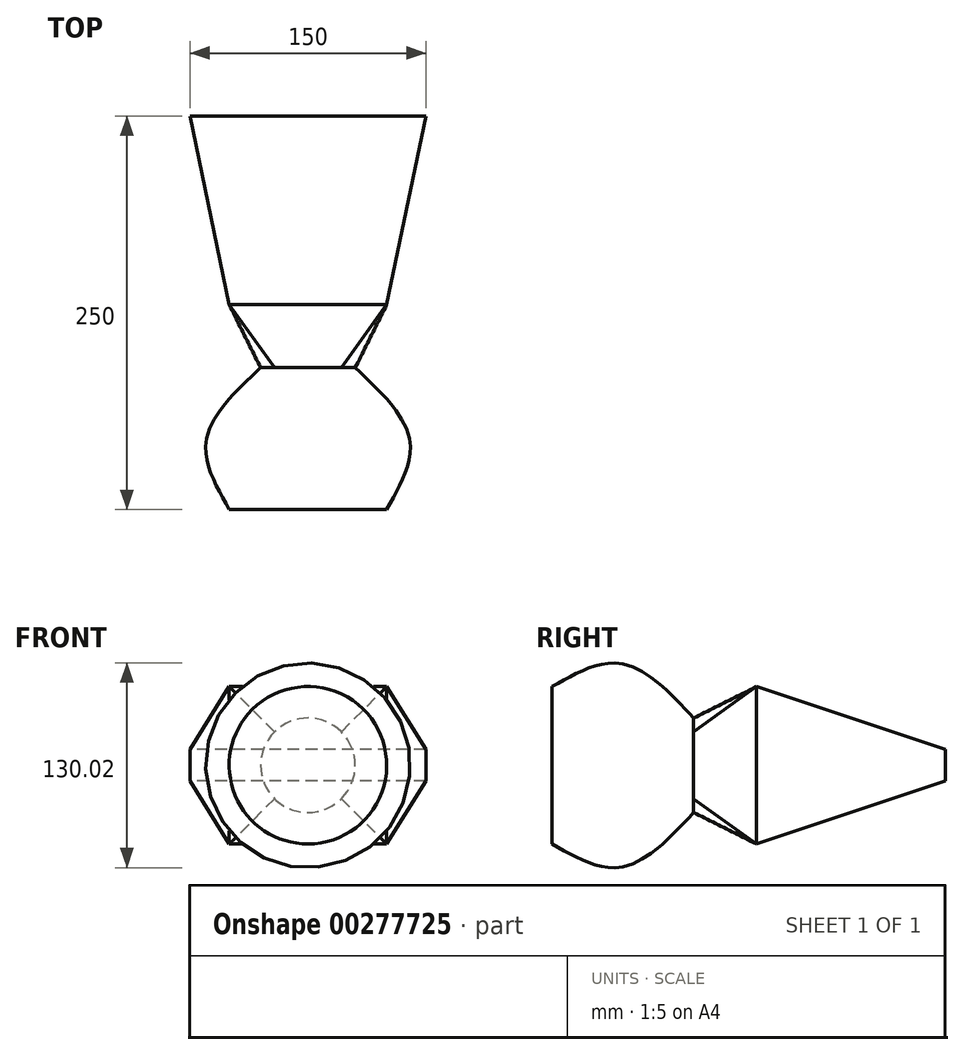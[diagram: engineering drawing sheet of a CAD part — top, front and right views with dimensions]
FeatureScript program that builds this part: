
annotation { "Feature Type Name" : "Feature", "Feature Type Description" : "" }
export const myFeature = defineFeature(function(context is Context, id is Id, definition is map)
    precondition{}
    {
        {
            var Q0;
            Q0=qCreatedBy(makeId("Front.planeOp"),FACE);
            var sketch = newSketch(context, id + "F0", { "sketchPlane" : qUnion([Q0])});
            skCircle(sketch, "E0", {"center": v(0, 0) * mm, "radius": 50 * mm});
            skSolve(sketch);
        }
        {
            var Q0;
            Q0=qCreatedBy(makeId("Front.planeOp"),FACE);
            cPlane(context, id + "F1", {"entities" : qUnion([Q0]), "cplaneType" : CPlaneType.OFFSET, "offset" : 40 * mm, "oppositeDirection" : true, "width" : 150 * mm, "height" : 150 * mm});
        }
        {
            var Q0;
            Q0=qCreatedBy(id+"F1.planeOp",FACE);
            var sketch = newSketch(context, id + "F2", { "sketchPlane" : qUnion([Q0])});
            skCircle(sketch, "E1", {"center": v(0, 0) * mm, "radius": 65 * mm});
            skSolve(sketch);
        }
        {
            var Q0;
            Q0=qCreatedBy(id+"F1.planeOp",FACE);
            cPlane(context, id + "F3", {"entities" : qUnion([Q0]), "cplaneType" : CPlaneType.OFFSET, "offset" : 50 * mm, "oppositeDirection" : true, "width" : 150 * mm, "height" : 150 * mm});
        }
        {
            var Q0;
            Q0=qCreatedBy(id+"F3.planeOp",FACE);
            var sketch = newSketch(context, id + "F4", { "sketchPlane" : qUnion([Q0])});
            skCircle(sketch, "E2", {"center": v(0, 0) * mm, "radius": 30 * mm});
            skSolve(sketch);
        }
        {
            var Q0;
            Q0=makeQuery(id+"F0.imprint","IMPRINT",FACE,{"disambiguationData":[TD([[makeQuery(id+"F0.imprint","IMPRINT",EDGE,{"derivedFrom":sQuery(id+"F0.wireOp",EDGE,"E0")}),1.0]])]});
            var Q1;
            Q1=makeQuery(id+"F2.imprint","IMPRINT",FACE,{"disambiguationData":[TD([[makeQuery(id+"F2.imprint","IMPRINT",EDGE,{"derivedFrom":sQuery(id+"F2.wireOp",EDGE,"E1")}),1.0]])]});
            var Q2;
            Q2=makeQuery(id+"F4.imprint","IMPRINT",FACE,{"disambiguationData":[TD([[makeQuery(id+"F4.imprint","IMPRINT",EDGE,{"derivedFrom":sQuery(id+"F4.wireOp",EDGE,"E2")}),1.0]])]});
            loft(context, id + "F5", {"sheetProfilesArray" : [{ "sheetProfileEntities" : qUnion([Q0]) }, { "sheetProfileEntities" : qUnion([Q1]) }, { "sheetProfileEntities" : qUnion([Q2]) }]});
        }
        {
            var Q0;
            Q0=qCreatedBy(id+"F3.planeOp",FACE);
            cPlane(context, id + "F6", {"entities" : qUnion([Q0]), "cplaneType" : CPlaneType.OFFSET, "offset" : 40 * mm, "oppositeDirection" : true, "width" : 150 * mm, "height" : 150 * mm});
        }
        {
            var Q0;
            Q0=qCreatedBy(id+"F6.planeOp",FACE);
            cPlane(context, id + "F7", {"entities" : qUnion([Q0]), "cplaneType" : CPlaneType.OFFSET, "offset" : 120 * mm, "oppositeDirection" : true, "width" : 150 * mm, "height" : 150 * mm});
        }
        {
            var Q0;
            Q0=qCreatedBy(id+"F6.planeOp",FACE);
            var sketch = newSketch(context, id + "F8", { "sketchPlane" : qUnion([Q0])});
            skLineSegment(sketch, "E3.bottom", {"start": v(50, -50) * mm, "end": v(-50, -50) * mm});
            skLineSegment(sketch, "E3.top", {"start": v(50, 50) * mm, "end": v(-50, 50) * mm});
            skLineSegment(sketch, "E3.left", {"start": v(50, -50) * mm, "end": v(50, 50) * mm});
            skLineSegment(sketch, "E3.right", {"start": v(-50, -50) * mm, "end": v(-50, 50) * mm});
            skPoint(sketch, "E3.middle", {"position": v(0, 0) * mm});
            skSolve(sketch);
        }
        {
            var Q0;
            Q0=qCreatedBy(id+"F7.planeOp",FACE);
            var sketch = newSketch(context, id + "F9", { "sketchPlane" : qUnion([Q0])});
            skLineSegment(sketch, "E4.bottom", {"start": v(75, 10) * mm, "end": v(-75, 10) * mm});
            skLineSegment(sketch, "E4.top", {"start": v(75, -10) * mm, "end": v(-75, -10) * mm});
            skLineSegment(sketch, "E4.left", {"start": v(75, 10) * mm, "end": v(75, -10) * mm});
            skLineSegment(sketch, "E4.right", {"start": v(-75, 10) * mm, "end": v(-75, -10) * mm});
            skPoint(sketch, "E4.middle", {"position": v(0, 0) * mm});
            skSolve(sketch);
        }
        {
            var Q1;
            Q1=makeQuery(id+"F5.opLoft","CAP_FACE",FACE,{"disambiguationData":[OSD([makeQuery(id+"F4.imprint","IMPRINT",FACE,{"disambiguationData":[TD([[makeQuery(id+"F4.imprint","IMPRINT",EDGE,{"derivedFrom":sQuery(id+"F4.wireOp",EDGE,"E2")}),1.0]])]})])],"isStart":true});
            var Q2;
            Q2=makeQuery(id+"F8.imprint","IMPRINT",FACE,{"disambiguationData":[TD([[makeQuery(id+"F8.imprint","IMPRINT",EDGE,{"derivedFrom":sQuery(id+"F8.wireOp",EDGE,"E3.bottom")}),-1.0]])]});
            loft(context, id + "F10", {"operationType" : NewBodyOperationType.ADD, "sheetProfilesArray" : [{ "sheetProfileEntities" : qUnion([Q1]) }, { "sheetProfileEntities" : qUnion([Q2]) }]});
        }
        {
            var Q1;
            Q1=makeQuery(id+"F10.opLoft","CAP_FACE",FACE,{"disambiguationData":[OSD([makeQuery(id+"F8.imprint","IMPRINT",FACE,{"disambiguationData":[TD([[makeQuery(id+"F8.imprint","IMPRINT",EDGE,{"derivedFrom":sQuery(id+"F8.wireOp",EDGE,"E3.bottom")}),-1.0]])]})])],"isStart":true});
            var Q2;
            Q2=makeQuery(id+"F9.imprint","IMPRINT",FACE,{"disambiguationData":[TD([[makeQuery(id+"F9.imprint","IMPRINT",EDGE,{"derivedFrom":sQuery(id+"F9.wireOp",EDGE,"E4.bottom")}),1.0]])]});
            loft(context, id + "F11", {"operationType" : NewBodyOperationType.ADD, "sheetProfilesArray" : [{ "sheetProfileEntities" : qUnion([Q1]) }, { "sheetProfileEntities" : qUnion([Q2]) }]});
        }
    });
